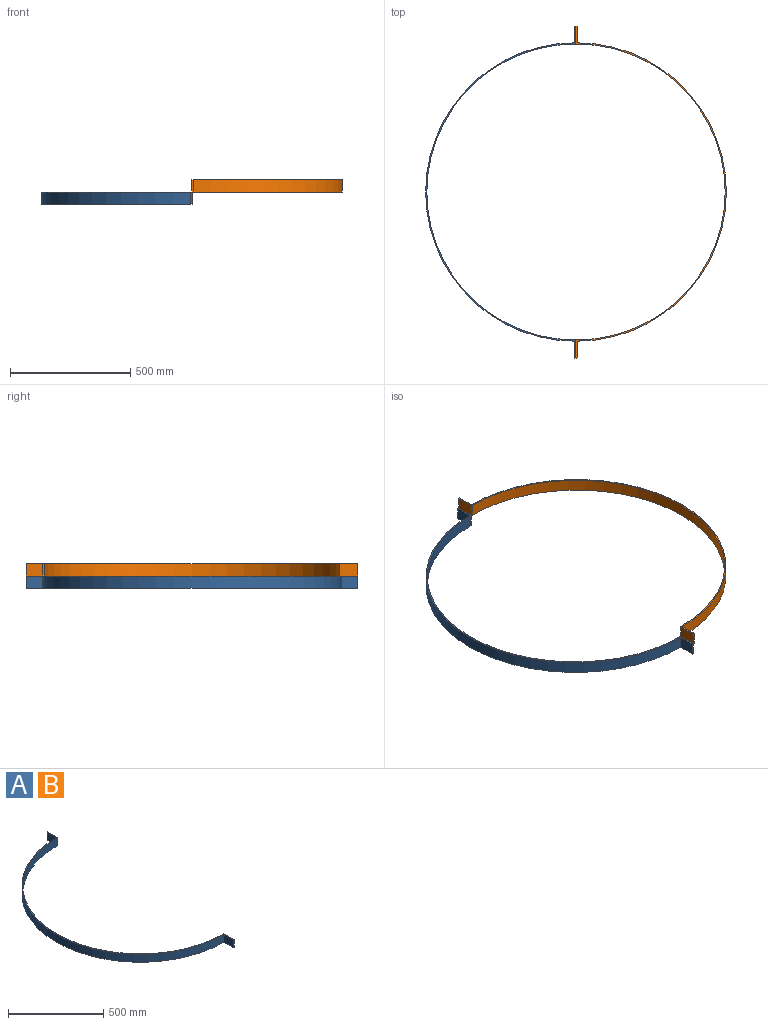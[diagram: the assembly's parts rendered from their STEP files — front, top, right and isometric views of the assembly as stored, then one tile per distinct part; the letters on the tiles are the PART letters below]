
ASSEMBLY  parts=2 mates=1
PART A: 12 faces, bbox 625x1380x50 mm
  f0: cylinder r=620mm len=1240mm, axis (0,0,-1), area 97389.4mm2, adj f1,f6,f7,f8
  f1: plane 70x50mm, normal (-1,0,0), area 3500mm2, adj f0,f2,f6,f7
  f2: plane 50x5mm, normal (0,-1,0), area 250mm2, adj f1,f3,f6,f7
  f3: plane 75x50mm, normal (1,0,0), area 3750mm2, adj f2,f4,f6,f7
  f4: plane 50x5mm, normal (0,1,0), area 250mm2, adj f3,f5,f6,f7
  f5: cylinder r=615mm len=1230mm, axis (0,0,-1), area 96604mm2, adj f4,f6,f7,f11
  f6: plane 1380x625mm, normal (0,0,1), area 10449.7mm2, adj f0,f1,f2,f3,f4,f5,f8,f9
  f7: plane 1380x625mm, normal (0,0,-1), area 10449.7mm2, adj f0,f1,f2,f3,f4,f5,f8,f9
  f8: plane 70x50mm, normal (-1,0,0), area 3500mm2, adj f0,f6,f7,f9
  f9: plane 50x5mm, normal (0,1,0), area 250mm2, adj f6,f7,f8,f10
  f10: plane 75x50mm, normal (1,0,0), area 3750mm2, adj f6,f7,f9,f11
  f11: plane 50x5mm, normal (0,-1,0), area 250mm2, adj f5,f6,f7,f10
PART B: same geometry as A
PLACE A at identity
PLACE B rot(axis=(0,1,0),180deg) t=(10,0,100)mm
MATE fastened B.f3 <-> A.f3  axis (-1,0,0) through (5,-652.5,75)mm
